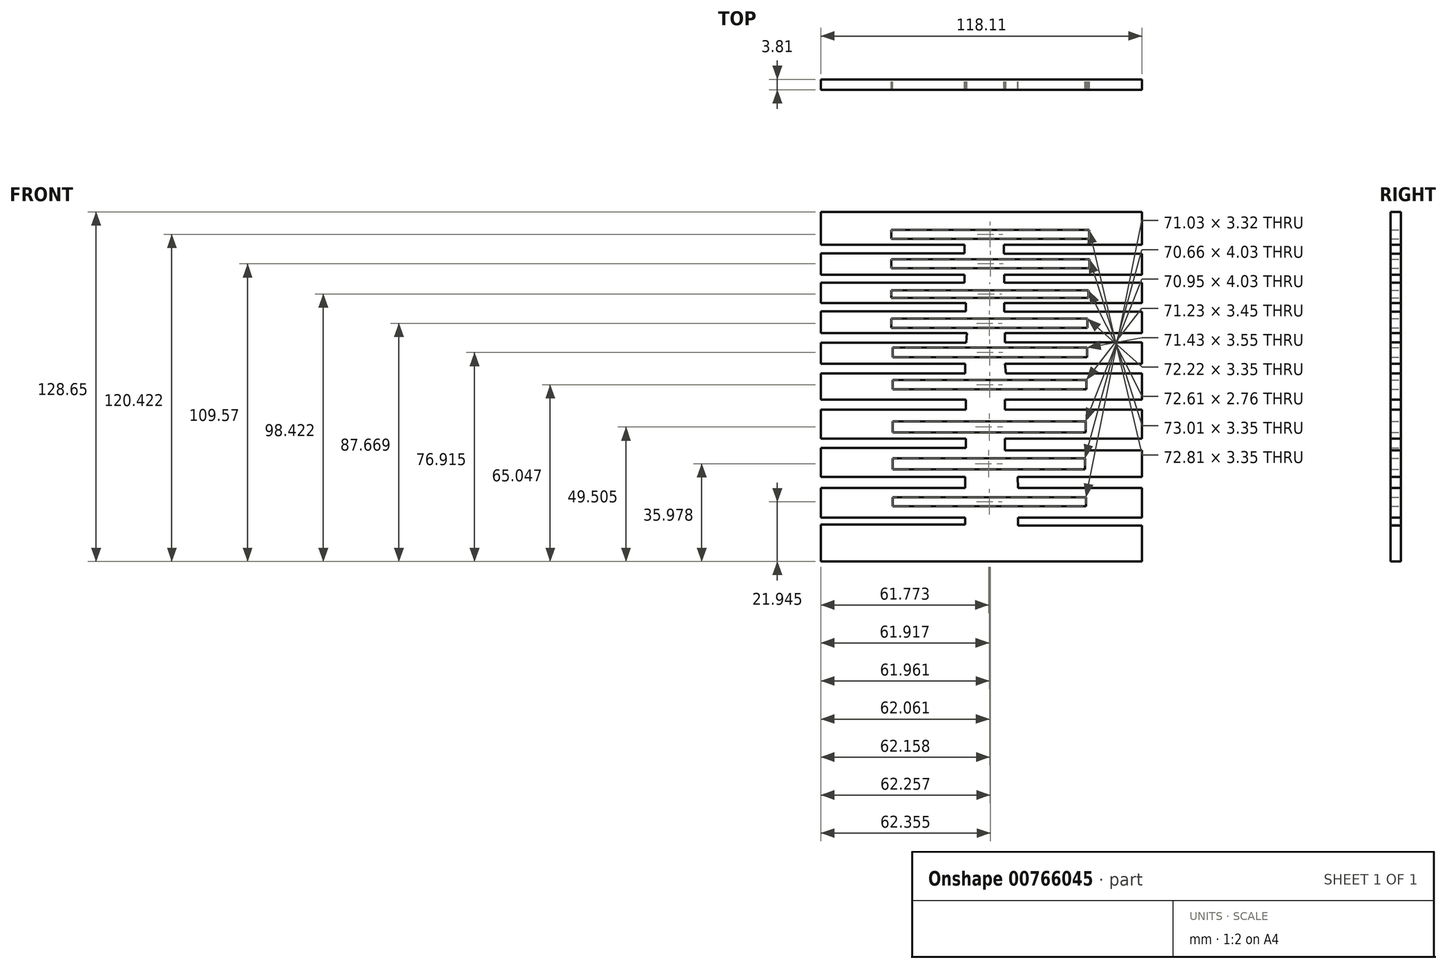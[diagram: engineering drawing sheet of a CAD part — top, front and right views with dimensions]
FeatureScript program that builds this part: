
annotation { "Feature Type Name" : "Feature", "Feature Type Description" : "" }
export const myFeature = defineFeature(function(context is Context, id is Id, definition is map)
    precondition{}
    {
        {
            var Q0;
            Q0=qCreatedBy(makeId("Front.planeOp"),FACE);
            var sketch = newSketch(context, id + "F0", { "sketchPlane" : qUnion([Q0])});
            skLineSegment(sketch, "E0.bottom", {"start": v(-61.27, 59.43) * mm, "end": v(56.84, 59.43) * mm});
            skLineSegment(sketch, "E0.top", {"start": v(-61.27, -69.22) * mm, "end": v(56.84, -69.22) * mm});
            skLineSegment(sketch, "E0.left", {"start": v(-61.27, 59.43) * mm, "end": v(-61.27, 47.35) * mm});
            skLineSegment(sketch, "E0.right", {"start": v(56.84, 59.43) * mm, "end": v(56.84, 47.35) * mm});
            skLineSegment(sketch, "E1.bottom", {"start": v(-34.83, -45.62) * mm, "end": v(36.2, -45.62) * mm});
            skLineSegment(sketch, "E1.top", {"start": v(-34.83, -48.93) * mm, "end": v(36.2, -48.93) * mm});
            skLineSegment(sketch, "E1.left", {"start": v(-34.83, -45.62) * mm, "end": v(-34.83, -48.93) * mm});
            skLineSegment(sketch, "E1.right", {"start": v(36.2, -45.62) * mm, "end": v(36.2, -48.93) * mm});
            skLineSegment(sketch, "E2.bottom", {"start": v(56.84, -38.13) * mm, "end": v(11.08, -38.13) * mm});
            skLineSegment(sketch, "E2.top", {"start": v(56.84, -42.16) * mm, "end": v(11.2, -42.16) * mm});
            skLineSegment(sketch, "E2.right", {"start": v(11.08, -38.13) * mm, "end": v(11.2, -42.16) * mm});
            skLineSegment(sketch, "E3.bottom", {"start": v(-61.27, -38.13) * mm, "end": v(-8.2, -38.13) * mm});
            skLineSegment(sketch, "E3.top", {"start": v(-61.27, -42.16) * mm, "end": v(-8.2, -42.16) * mm});
            skLineSegment(sketch, "E3.right", {"start": v(-8.2, -38.13) * mm, "end": v(-8.2, -42.16) * mm});
            skLineSegment(sketch, "E4.trimOffspring", {"start": v(-61.27, -42.16) * mm, "end": v(-61.27, -53.08) * mm});
            skLineSegment(sketch, "E5.trimOffspring", {"start": v(56.84, -42.16) * mm, "end": v(56.84, -53.08) * mm});
            skLineSegment(sketch, "E6.bottom", {"start": v(-34.83, -31.23) * mm, "end": v(35.83, -31.23) * mm});
            skLineSegment(sketch, "E6.top", {"start": v(-34.83, -35.26) * mm, "end": v(35.83, -35.26) * mm});
            skLineSegment(sketch, "E6.left", {"start": v(-34.83, -31.23) * mm, "end": v(-34.83, -35.26) * mm});
            skLineSegment(sketch, "E6.right", {"start": v(35.83, -31.23) * mm, "end": v(35.83, -35.26) * mm});
            skLineSegment(sketch, "E7.bottom", {"start": v(56.84, -24.03) * mm, "end": v(6.48, -24.03) * mm});
            skLineSegment(sketch, "E7.top", {"start": v(56.84, -28.35) * mm, "end": v(6.48, -28.35) * mm});
            skLineSegment(sketch, "E7.right", {"start": v(6.48, -24.03) * mm, "end": v(6.48, -28.35) * mm});
            skLineSegment(sketch, "E8.bottom", {"start": v(-61.27, -24.03) * mm, "end": v(-7.91, -24.03) * mm});
            skLineSegment(sketch, "E8.top", {"start": v(-61.27, -27.49) * mm, "end": v(-7.91, -27.49) * mm});
            skLineSegment(sketch, "E8.right", {"start": v(-7.91, -24.03) * mm, "end": v(-7.91, -27.49) * mm});
            skLineSegment(sketch, "E9.bottom", {"start": v(-34.83, -17.7) * mm, "end": v(36.12, -17.7) * mm});
            skLineSegment(sketch, "E9.top", {"start": v(-34.83, -21.73) * mm, "end": v(36.12, -21.73) * mm});
            skLineSegment(sketch, "E9.left", {"start": v(-34.83, -17.7) * mm, "end": v(-34.83, -21.73) * mm});
            skLineSegment(sketch, "E9.right", {"start": v(36.12, -17.7) * mm, "end": v(36.12, -21.73) * mm});
            skLineSegment(sketch, "E10.bottom", {"start": v(-7.91, -9.64) * mm, "end": v(-61.27, -9.64) * mm});
            skLineSegment(sketch, "E10.top", {"start": v(-7.91, -13.38) * mm, "end": v(-61.27, -13.38) * mm});
            skLineSegment(sketch, "E10.left", {"start": v(-7.91, -9.64) * mm, "end": v(-7.91, -13.38) * mm});
            skLineSegment(sketch, "E11.bottom", {"start": v(6.48, -9.64) * mm, "end": v(56.84, -9.64) * mm});
            skLineSegment(sketch, "E11.top", {"start": v(6.48, -13.38) * mm, "end": v(56.84, -13.38) * mm});
            skLineSegment(sketch, "E11.left", {"start": v(6.48, -9.64) * mm, "end": v(6.48, -13.38) * mm});
            skLineSegment(sketch, "E12.trimOffspring", {"start": v(-61.27, -13.38) * mm, "end": v(-61.27, -24.03) * mm});
            skLineSegment(sketch, "E13.trimOffspring", {"start": v(56.84, -13.38) * mm, "end": v(56.84, -24.03) * mm});
            skLineSegment(sketch, "E14.bottom", {"start": v(-34.83, -2.45) * mm, "end": v(36.4, -2.45) * mm});
            skLineSegment(sketch, "E14.top", {"start": v(-34.83, -5.9) * mm, "end": v(36.4, -5.9) * mm});
            skLineSegment(sketch, "E14.left", {"start": v(-34.83, -2.45) * mm, "end": v(-34.83, -5.9) * mm});
            skLineSegment(sketch, "E14.right", {"start": v(36.4, -2.45) * mm, "end": v(36.4, -5.9) * mm});
            skLineSegment(sketch, "E15.bottom", {"start": v(-61.27, 3.6) * mm, "end": v(-8.2, 3.6) * mm});
            skLineSegment(sketch, "E15.top", {"start": v(-61.27, 0) * mm, "end": v(-8.2, 0) * mm});
            skLineSegment(sketch, "E15.right", {"start": v(-8.2, 3.6) * mm, "end": v(-8.2, 0) * mm});
            skLineSegment(sketch, "E16.trimOffspring", {"start": v(-61.27, 0) * mm, "end": v(-61.27, -9.64) * mm});
            skLineSegment(sketch, "E17.bottom", {"start": v(56.84, 3.6) * mm, "end": v(6.48, 3.6) * mm});
            skLineSegment(sketch, "E17.top", {"start": v(56.84, 0) * mm, "end": v(6.76, 0) * mm});
            skLineSegment(sketch, "E17.right", {"start": v(6.48, 3.6) * mm, "end": v(6.76, 0) * mm});
            skLineSegment(sketch, "E18.trimOffspring", {"start": v(56.84, 0) * mm, "end": v(56.84, -9.64) * mm});
            skLineSegment(sketch, "E19.trimOffspring", {"start": v(56.84, -28.35) * mm, "end": v(56.84, -38.13) * mm});
            skLineSegment(sketch, "E20.trimOffspring", {"start": v(-61.27, -27.49) * mm, "end": v(-61.27, -38.13) * mm});
            skLineSegment(sketch, "E21.bottom", {"start": v(-34.83, 9.47) * mm, "end": v(36.6, 9.47) * mm});
            skLineSegment(sketch, "E21.top", {"start": v(-34.83, 5.92) * mm, "end": v(36.6, 5.92) * mm});
            skLineSegment(sketch, "E21.left", {"start": v(-34.83, 9.47) * mm, "end": v(-34.83, 5.92) * mm});
            skLineSegment(sketch, "E21.right", {"start": v(36.6, 9.47) * mm, "end": v(36.6, 5.92) * mm});
            skLineSegment(sketch, "E22.bottom", {"start": v(-61.27, 14.8) * mm, "end": v(-7.6, 14.8) * mm});
            skLineSegment(sketch, "E22.top", {"start": v(-61.27, 11.25) * mm, "end": v(-7.8, 11.25) * mm});
            skLineSegment(sketch, "E22.right", {"start": v(-7.6, 14.8) * mm, "end": v(-7.8, 11.25) * mm});
            skLineSegment(sketch, "E23.trimOffspring", {"start": v(-61.27, 11.25) * mm, "end": v(-61.27, 3.6) * mm});
            skLineSegment(sketch, "E24.bottom", {"start": v(56.84, 14.8) * mm, "end": v(6.41, 14.8) * mm});
            skLineSegment(sketch, "E24.top", {"start": v(56.84, 11.44) * mm, "end": v(6.41, 11.44) * mm});
            skLineSegment(sketch, "E24.right", {"start": v(6.41, 14.8) * mm, "end": v(6.41, 11.44) * mm});
            skLineSegment(sketch, "E25.trimOffspring", {"start": v(56.84, 11.44) * mm, "end": v(56.84, 3.6) * mm});
            skLineSegment(sketch, "E26.bottom", {"start": v(-35.42, 20.13) * mm, "end": v(36.8, 20.13) * mm});
            skLineSegment(sketch, "E26.top", {"start": v(-35.42, 16.77) * mm, "end": v(36.8, 16.77) * mm});
            skLineSegment(sketch, "E26.left", {"start": v(-35.42, 20.13) * mm, "end": v(-35.42, 16.77) * mm});
            skLineSegment(sketch, "E26.right", {"start": v(36.8, 20.13) * mm, "end": v(36.8, 16.77) * mm});
            skLineSegment(sketch, "E27.bottom", {"start": v(-61.27, 25.85) * mm, "end": v(-8, 25.85) * mm});
            skLineSegment(sketch, "E27.top", {"start": v(-61.27, 22.89) * mm, "end": v(-8, 22.89) * mm});
            skLineSegment(sketch, "E27.right", {"start": v(-8, 25.85) * mm, "end": v(-8, 22.89) * mm});
            skLineSegment(sketch, "E28.trimOffspring", {"start": v(-61.27, 22.89) * mm, "end": v(-61.27, 14.8) * mm});
            skLineSegment(sketch, "E29.bottom", {"start": v(56.84, 25.85) * mm, "end": v(6.22, 25.85) * mm});
            skLineSegment(sketch, "E29.top", {"start": v(56.84, 22.7) * mm, "end": v(6.22, 22.7) * mm});
            skLineSegment(sketch, "E29.right", {"start": v(6.22, 25.85) * mm, "end": v(6.22, 22.7) * mm});
            skLineSegment(sketch, "E30.trimOffspring", {"start": v(56.84, 22.7) * mm, "end": v(56.84, 14.8) * mm});
            skLineSegment(sketch, "E31.bottom", {"start": v(-35.42, 30.58) * mm, "end": v(37.2, 30.58) * mm});
            skLineSegment(sketch, "E31.top", {"start": v(-35.42, 27.82) * mm, "end": v(37.2, 27.82) * mm});
            skLineSegment(sketch, "E31.left", {"start": v(-35.42, 30.58) * mm, "end": v(-35.42, 27.82) * mm});
            skLineSegment(sketch, "E31.right", {"start": v(37.2, 30.58) * mm, "end": v(37.2, 27.82) * mm});
            skLineSegment(sketch, "E32.bottom", {"start": v(-61.27, 36.3) * mm, "end": v(-8.39, 36.3) * mm});
            skLineSegment(sketch, "E32.top", {"start": v(-61.27, 33.35) * mm, "end": v(-8.39, 33.35) * mm});
            skLineSegment(sketch, "E32.right", {"start": v(-8.39, 36.3) * mm, "end": v(-8.39, 33.35) * mm});
            skLineSegment(sketch, "E33.trimOffspring", {"start": v(-61.27, 33.35) * mm, "end": v(-61.27, 25.85) * mm});
            skLineSegment(sketch, "E34.bottom", {"start": v(56.84, 36.3) * mm, "end": v(6.22, 36.3) * mm});
            skLineSegment(sketch, "E34.top", {"start": v(56.84, 33.35) * mm, "end": v(6.22, 33.35) * mm});
            skLineSegment(sketch, "E34.right", {"start": v(6.22, 36.3) * mm, "end": v(6.22, 33.35) * mm});
            skLineSegment(sketch, "E35.trimOffspring", {"start": v(56.84, 33.35) * mm, "end": v(56.84, 25.85) * mm});
            skLineSegment(sketch, "E36.bottom", {"start": v(-35.42, 42.03) * mm, "end": v(37.59, 42.03) * mm});
            skLineSegment(sketch, "E36.top", {"start": v(-35.42, 38.67) * mm, "end": v(37.59, 38.67) * mm});
            skLineSegment(sketch, "E36.left", {"start": v(-35.42, 42.03) * mm, "end": v(-35.42, 38.67) * mm});
            skLineSegment(sketch, "E36.right", {"start": v(37.59, 42.03) * mm, "end": v(37.59, 38.67) * mm});
            skLineSegment(sketch, "E37.bottom", {"start": v(-61.27, 47.35) * mm, "end": v(-8.39, 47.35) * mm});
            skLineSegment(sketch, "E37.top", {"start": v(-61.27, 44.2) * mm, "end": v(-8.39, 44.2) * mm});
            skLineSegment(sketch, "E37.right", {"start": v(-8.39, 47.35) * mm, "end": v(-8.39, 44.2) * mm});
            skLineSegment(sketch, "E38.trimOffspring", {"start": v(-61.27, 44.2) * mm, "end": v(-61.27, 36.3) * mm});
            skLineSegment(sketch, "E39.bottom", {"start": v(56.84, 47.35) * mm, "end": v(6.02, 47.35) * mm});
            skLineSegment(sketch, "E39.top", {"start": v(56.84, 44) * mm, "end": v(6.02, 44) * mm});
            skLineSegment(sketch, "E39.right", {"start": v(6.02, 47.35) * mm, "end": v(6.02, 44) * mm});
            skLineSegment(sketch, "E40.trimOffspring", {"start": v(56.84, 44) * mm, "end": v(56.84, 36.3) * mm});
            skLineSegment(sketch, "E41.bottom", {"start": v(-35.42, 52.88) * mm, "end": v(37.4, 52.88) * mm});
            skLineSegment(sketch, "E41.top", {"start": v(-35.42, 49.53) * mm, "end": v(37.4, 49.53) * mm});
            skLineSegment(sketch, "E41.left", {"start": v(-35.42, 52.88) * mm, "end": v(-35.42, 49.53) * mm});
            skLineSegment(sketch, "E41.right", {"start": v(37.4, 52.88) * mm, "end": v(37.4, 49.53) * mm});
            skLineSegment(sketch, "E42.bottom", {"start": v(-8.2, -53.08) * mm, "end": v(-61.27, -53.08) * mm});
            skLineSegment(sketch, "E42.top", {"start": v(-8.2, -55.7) * mm, "end": v(-61.27, -55.7) * mm});
            skLineSegment(sketch, "E42.left", {"start": v(-8.2, -53.08) * mm, "end": v(-8.2, -55.7) * mm});
            skLineSegment(sketch, "E43.bottom", {"start": v(56.84, -53.08) * mm, "end": v(11.2, -53.08) * mm});
            skLineSegment(sketch, "E43.top", {"start": v(56.84, -56.04) * mm, "end": v(11.2, -56.04) * mm});
            skLineSegment(sketch, "E43.right", {"start": v(11.2, -53.08) * mm, "end": v(11.2, -56.04) * mm});
            skLineSegment(sketch, "E44.trimOffspring", {"start": v(-61.27, -55.7) * mm, "end": v(-61.27, -69.22) * mm});
            skLineSegment(sketch, "E45.trimOffspring", {"start": v(56.84, -56.04) * mm, "end": v(56.84, -69.22) * mm});
            skSolve(sketch);
        }
        {
            var Q0;
            Q0=makeQuery(id+"F0.imprint","IMPRINT",FACE,{"disambiguationData":[TD([[makeQuery(id+"F0.imprint","IMPRINT",EDGE,{"derivedFrom":sQuery(id+"F0.wireOp",EDGE,"E0.bottom")}),-1.0]])]});
            extrude(context, id + "F1", {"entities" : qUnion([Q0]), "depth" : 3.8 * mm, "offsetDistance" : 25.4 * mm});
        }
    });
